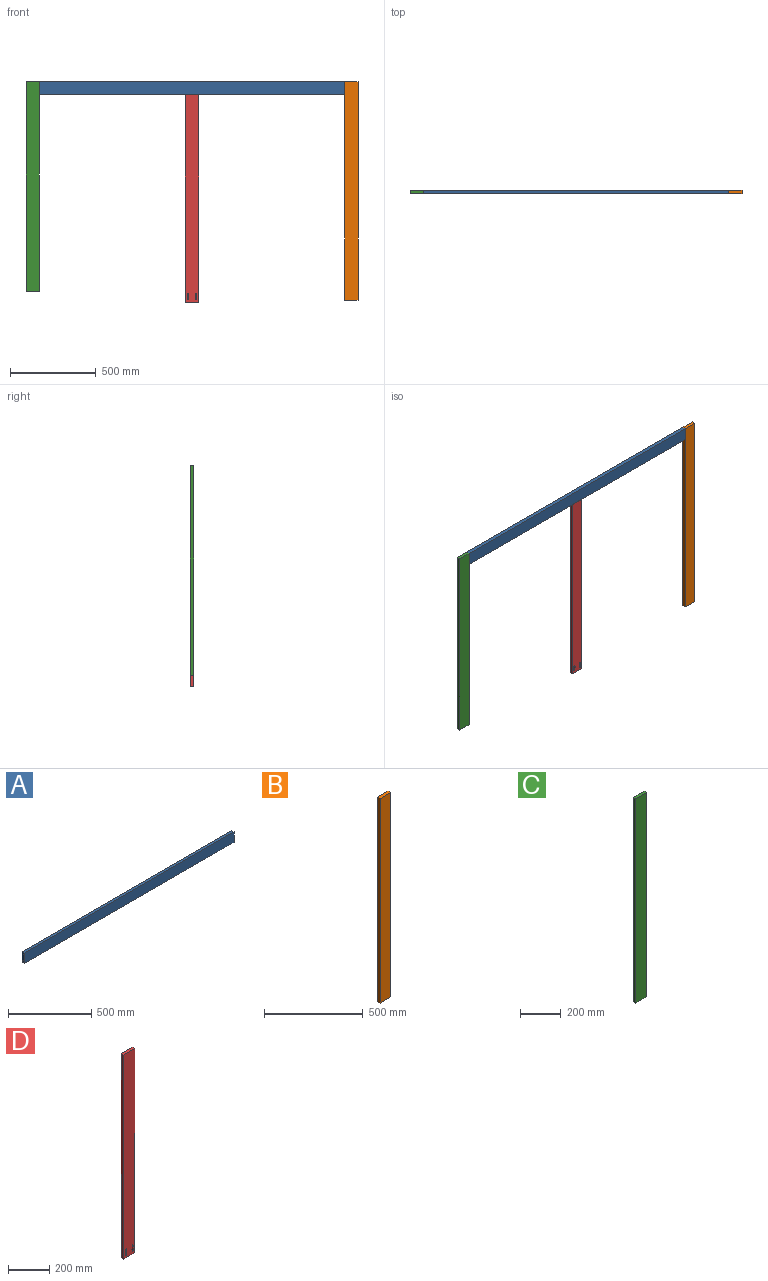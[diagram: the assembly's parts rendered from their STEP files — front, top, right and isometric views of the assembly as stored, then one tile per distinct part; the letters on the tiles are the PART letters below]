
ASSEMBLY  parts=4 mates=3
PART A: 22 faces, bbox 1778x28.3x76.2 mm
  f0: plane 1778x19.05mm, normal (0,0,-1), area 33870.9mm2, adj f1,f3,f4,f5
  f1: plane 76.2x19.05mm, normal (1,0,0), area 1451.6mm2, adj f0,f2,f4,f5
  f2: plane 1778x19.05mm, normal (0,0,1), area 33870.9mm2, adj f1,f3,f4,f5
  f3: plane 76.2x19.05mm, normal (-1,0,0), area 1451.6mm2, adj f0,f2,f4,f5
  f4: plane 1778x76.2mm, normal (0,-1,0), area 135483.6mm2, adj f0,f1,f2,f3
  f5: plane 1778x76.2mm, normal (0,1,0), area 134382.4mm2, adj f0,f1,f2,f3,f6,f10,f14,f18
  f6: cylinder r=4.76mm len=40.55mm, axis (0.97,-0.26,0), area 640.6mm2, adj f5,f7
  f7: plane 9.53x9.2mm, normal (-0.97,0.26,0), area 58.9mm2, adj f6,f9
  f8: plane 3.97x3.83mm, normal (-0.97,0.26,0), area 12.4mm2, adj f9
  f9: cylinder r=1.98mm len=13.29mm, axis (0.97,-0.26,0), area 158.3mm2, adj f7,f8
  f10: cylinder r=4.76mm len=40.55mm, axis (0.97,-0.26,0), area 640.6mm2, adj f5,f11
  f11: plane 9.53x9.2mm, normal (-0.97,0.26,0), area 58.9mm2, adj f10,f13
  f12: plane 3.97x3.83mm, normal (-0.97,0.26,0), area 12.4mm2, adj f13
  f13: cylinder r=1.98mm len=13.29mm, axis (0.97,-0.26,0), area 158.3mm2, adj f11,f12
  f14: cylinder r=4.76mm len=40.55mm, axis (-0.97,-0.26,0), area 640.6mm2, adj f5,f15
  f15: plane 9.53x9.2mm, normal (0.97,0.26,0), area 58.9mm2, adj f14,f17
  f16: plane 3.97x3.83mm, normal (0.97,0.26,0), area 12.4mm2, adj f17
  f17: cylinder r=1.98mm len=13.29mm, axis (-0.97,-0.26,0), area 158.3mm2, adj f15,f16
  f18: cylinder r=4.76mm len=40.55mm, axis (-0.97,-0.26,0), area 640.6mm2, adj f5,f19
  f19: plane 9.53x9.2mm, normal (0.97,0.26,0), area 58.9mm2, adj f18,f21
  f20: plane 3.97x3.83mm, normal (0.97,0.26,0), area 12.4mm2, adj f21
  f21: cylinder r=1.98mm len=13.29mm, axis (-0.97,-0.26,0), area 158.3mm2, adj f19,f20
PART B: 6 faces, bbox 76.2x19.1x1270 mm
  f0: plane 1270x19.05mm, normal (-1,0,0), area 24193.5mm2, adj f1,f3,f4,f5
  f1: plane 76.2x19.05mm, normal (0,0,-1), area 1451.6mm2, adj f0,f2,f4,f5
  f2: plane 1270x19.05mm, normal (1,0,0), area 24193.5mm2, adj f1,f3,f4,f5
  f3: plane 76.2x19.05mm, normal (0,0,1), area 1451.6mm2, adj f0,f2,f4,f5
  f4: plane 1270x76.2mm, normal (0,-1,0), area 96774mm2, adj f0,f1,f2,f3
  f5: plane 1270x76.2mm, normal (0,1,0), area 96774mm2, adj f0,f1,f2,f3
PART C: 6 faces, bbox 76.2x19.1x1219.2 mm
  f0: plane 76.2x19.05mm, normal (0,0,-1), area 1451.6mm2, adj f1,f3,f4,f5
  f1: plane 1219.2x19.05mm, normal (1,0,0), area 23225.8mm2, adj f0,f2,f4,f5
  f2: plane 76.2x19.05mm, normal (0,0,1), area 1451.6mm2, adj f1,f3,f4,f5
  f3: plane 1219.2x19.05mm, normal (-1,0,0), area 23225.8mm2, adj f0,f2,f4,f5
  f4: plane 1219.2x76.2mm, normal (0,-1,0), area 92903mm2, adj f0,f1,f2,f3
  f5: plane 1219.2x76.2mm, normal (0,1,0), area 92903mm2, adj f0,f1,f2,f3
PART D: 14 faces, bbox 76.2x28.3x1206.5 mm
  f0: plane 1206.5x19.05mm, normal (1,0,0), area 22983.8mm2, adj f1,f3,f4,f5
  f1: plane 76.2x19.05mm, normal (0,0,1), area 1451.6mm2, adj f0,f2,f4,f5
  f2: plane 1206.5x19.05mm, normal (-1,0,0), area 22983.8mm2, adj f1,f3,f4,f5
  f3: plane 76.2x19.05mm, normal (0,0,-1), area 1451.6mm2, adj f0,f2,f4,f5
  f4: plane 1206.5x76.2mm, normal (0,-1,0), area 91384.7mm2, adj f0,f1,f2,f3,f6,f10
  f5: plane 1206.5x76.2mm, normal (0,1,0), area 91935.3mm2, adj f0,f1,f2,f3
  f6: cylinder r=4.76mm len=40.55mm, axis (0,0.26,-0.97), area 640.6mm2, adj f4,f7
  f7: plane 9.53x9.2mm, normal (0,-0.26,0.97), area 58.9mm2, adj f6,f9
  f8: plane 3.97x3.83mm, normal (0,-0.26,0.97), area 12.4mm2, adj f9
  f9: cylinder r=1.98mm len=13.29mm, axis (0,0.26,-0.97), area 158.3mm2, adj f7,f8
  f10: cylinder r=4.76mm len=40.55mm, axis (0,0.26,-0.97), area 640.6mm2, adj f4,f11
  f11: plane 9.53x9.2mm, normal (0,-0.26,0.97), area 58.9mm2, adj f10,f13
  f12: plane 3.97x3.83mm, normal (0,-0.26,0.97), area 12.4mm2, adj f13
  f13: cylinder r=1.98mm len=13.29mm, axis (0,0.26,-0.97), area 158.3mm2, adj f11,f12
PLACE A t=(185,565.92,1648.59)mm
PLACE B t=(246.35,565.92,1735.65)mm
PLACE C t=(190.77,565.92,1786.45)mm
PLACE D t=(212.46,565.92,1682.59)mm
MATE fastened A.f3 <-> C.f1  axis (-1,0,0) through (-635.48,556.4,2529.45)mm
MATE fastened B.f0 <-> A.f1  axis (-1,0,0) through (1142.52,546.87,2529.45)mm
MATE fastened D.f4 <-> A.f4  axis (0,-1,0) through (253.52,546.87,2453.25)mm
